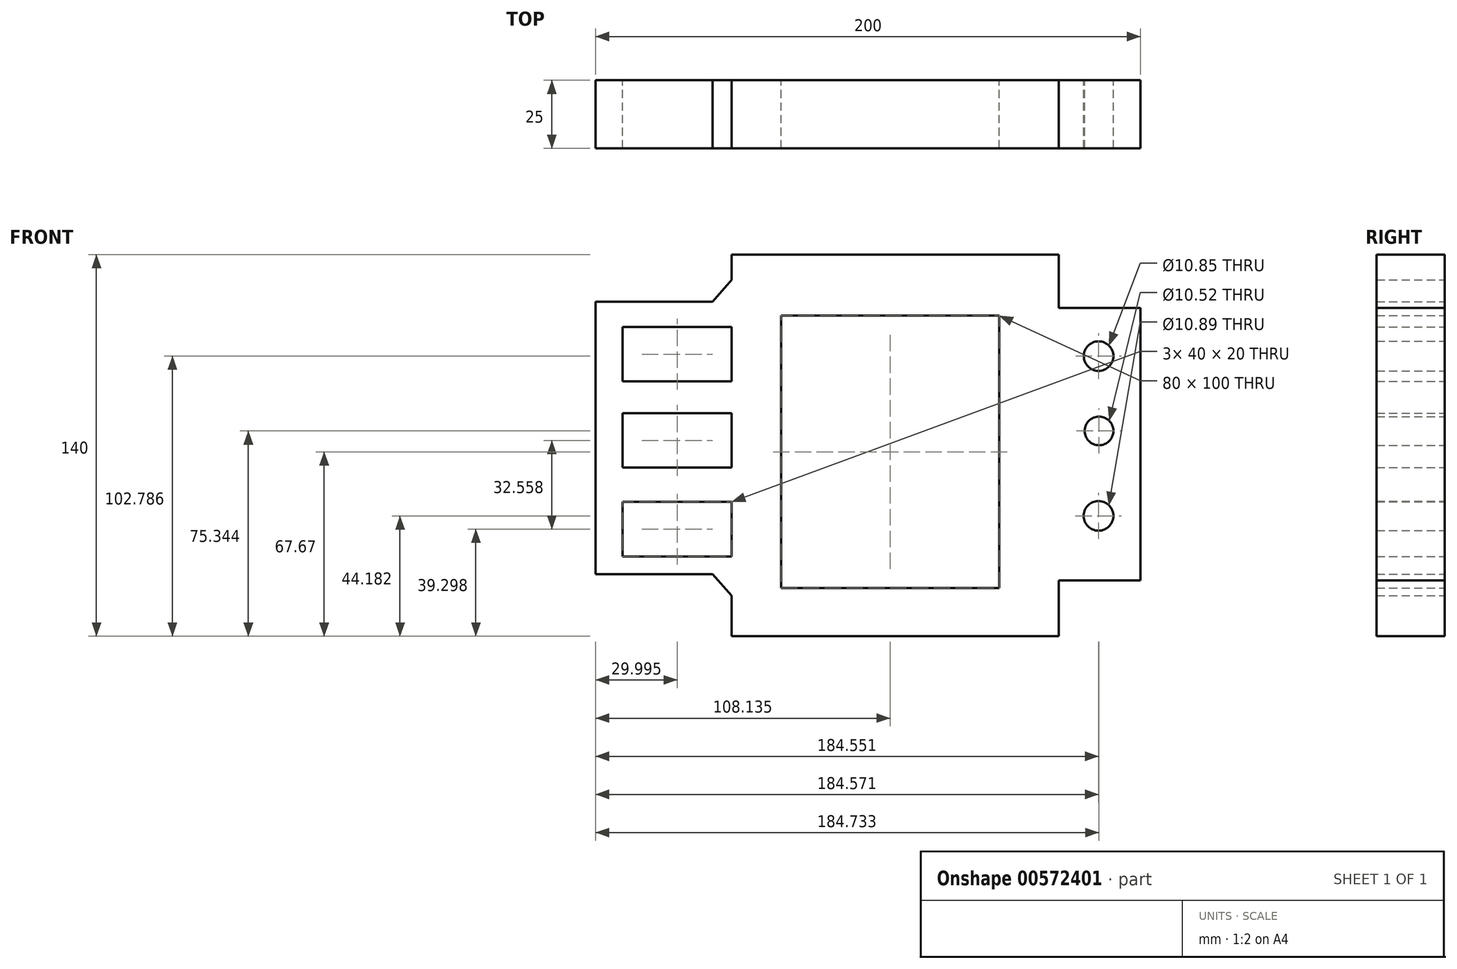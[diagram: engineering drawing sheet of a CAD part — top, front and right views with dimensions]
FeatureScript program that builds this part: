
annotation { "Feature Type Name" : "Feature", "Feature Type Description" : "" }
export const myFeature = defineFeature(function(context is Context, id is Id, definition is map)
    precondition{}
    {
        {
            var Q0;
            Q0=qCreatedBy(makeId("Front.planeOp"),FACE);
            var sketch = newSketch(context, id + "F0", { "sketchPlane" : qUnion([Q0])});
            skLineSegment(sketch, "E0", {"start": v(-163, -53.92) * mm, "end": v(-43, -53.92) * mm});
            skLineSegment(sketch, "E1", {"start": v(-43, -53.92) * mm, "end": v(-43, -33.46) * mm});
            skLineSegment(sketch, "E2", {"start": v(-43, -33.46) * mm, "end": v(-13, -33.46) * mm});
            skLineSegment(sketch, "E3", {"start": v(-13, -33.46) * mm, "end": v(-13, 66.54) * mm});
            skLineSegment(sketch, "E4", {"start": v(-13, 66.54) * mm, "end": v(-43, 66.54) * mm});
            skLineSegment(sketch, "E5", {"start": v(-43, 66.54) * mm, "end": v(-43, 86.08) * mm});
            skLineSegment(sketch, "E6", {"start": v(-43, 86.08) * mm, "end": v(-163, 86.08) * mm});
            skLineSegment(sketch, "E7", {"start": v(-163, 86.08) * mm, "end": v(-163, 76.77) * mm});
            skLineSegment(sketch, "E8", {"start": v(-163, 76.77) * mm, "end": v(-169.97, 68.87) * mm});
            skLineSegment(sketch, "E9", {"start": v(-169.97, 68.87) * mm, "end": v(-213, 68.87) * mm});
            skLineSegment(sketch, "E10", {"start": v(-213, 68.87) * mm, "end": v(-213, -31.13) * mm});
            skLineSegment(sketch, "E11", {"start": v(-213, -31.13) * mm, "end": v(-169.97, -31.13) * mm});
            skLineSegment(sketch, "E12", {"start": v(-169.97, -31.13) * mm, "end": v(-163, -39.04) * mm});
            skLineSegment(sketch, "E13", {"start": v(-163, -39.04) * mm, "end": v(-163, -53.92) * mm});
            skLineSegment(sketch, "E14.bottom", {"start": v(-144.86, 63.75) * mm, "end": v(-64.86, 63.75) * mm});
            skLineSegment(sketch, "E14.top", {"start": v(-144.86, -36.25) * mm, "end": v(-64.86, -36.25) * mm});
            skLineSegment(sketch, "E14.left", {"start": v(-144.86, 63.75) * mm, "end": v(-144.86, -36.25) * mm});
            skLineSegment(sketch, "E14.right", {"start": v(-64.86, 63.75) * mm, "end": v(-64.86, -36.25) * mm});
            skLineSegment(sketch, "E15.bottom", {"start": v(-203, 27.94) * mm, "end": v(-175.09, 27.94) * mm});
            skLineSegment(sketch, "E15.top", {"start": v(-203, 7.94) * mm, "end": v(-175.09, 7.94) * mm});
            skLineSegment(sketch, "E15.left", {"start": v(-203, 27.94) * mm, "end": v(-203, 7.94) * mm});
            skPoint(sketch, "E16.firstSnap0", {"position": v(-203, 17.94) * mm});
            skLineSegment(sketch, "E16.bottom", {"start": v(-203, 59.56) * mm, "end": v(-163, 59.56) * mm});
            skLineSegment(sketch, "E16.top", {"start": v(-203, 39.56) * mm, "end": v(-163, 39.56) * mm});
            skLineSegment(sketch, "E16.left", {"start": v(-203, 59.56) * mm, "end": v(-203, 39.56) * mm});
            skLineSegment(sketch, "E16.right", {"start": v(-163, 59.56) * mm, "end": v(-163, 39.56) * mm});
            skLineSegment(sketch, "E17.bottom", {"start": v(-203, 27.94) * mm, "end": v(-163, 27.94) * mm});
            skLineSegment(sketch, "E17.top", {"start": v(-203, 7.94) * mm, "end": v(-163, 7.94) * mm});
            skLineSegment(sketch, "E17.right", {"start": v(-163, 27.94) * mm, "end": v(-163, 7.94) * mm});
            skLineSegment(sketch, "E18.bottom", {"start": v(-203, -4.62) * mm, "end": v(-163, -4.62) * mm});
            skLineSegment(sketch, "E18.top", {"start": v(-203, -24.62) * mm, "end": v(-163, -24.62) * mm});
            skLineSegment(sketch, "E18.left", {"start": v(-203, -4.62) * mm, "end": v(-203, -24.62) * mm});
            skLineSegment(sketch, "E18.right", {"start": v(-163, -4.62) * mm, "end": v(-163, -24.62) * mm});
            skCircle(sketch, "E19", {"center": v(-28.42, 48.87) * mm, "radius": 5.42 * mm});
            skCircle(sketch, "E20", {"center": v(-28.26, 21.42) * mm, "radius": 5.26 * mm});
            skCircle(sketch, "E21", {"center": v(-28.44, -9.74) * mm, "radius": 5.44 * mm});
            skSolve(sketch);
        }
        {
            var Q0;
            Q0 = qSketchRegion(id + "F0", true);
            extrude(context, id + "F1", {"entities" : qUnion([Q0]), "depth" : 25 * mm, "offsetDistance" : 25 * mm});
        }
    });
